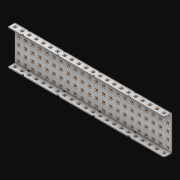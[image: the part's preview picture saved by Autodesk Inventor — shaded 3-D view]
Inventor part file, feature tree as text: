
AUTODESK INVENTOR PART (.ipt)
format: ipt  version: 2021 (Build 250183000, 183)  size: 3,487,744 bytes
history: native  units: in
note: dims shown in document units (in); Inventor stores cm internally (conversion verified against a paired STEP export)
features: extrude x155, other x154, sketch x4, thicken_offset x3, pattern_linear x3, imported_body x1
ambient origin geometry x8: Origin, YZ Plane, XZ Plane, XY Plane, X Axis, Y Axis, Z Axis, Center Point
bodies: Solid1 (feature_tree)
feature tree (320):
  thicken_offset  "Thicken1"
  thicken_offset  "Thicken2"
  thicken_offset  "Thicken3"
  pattern_linear  "Rectangular Pattern1"  Spacing1=0.001in  [1 undecoded]
  pattern_linear  "Rectangular Pattern2"  Spacing1=0.001in  [1 undecoded]
  pattern_linear  "Rectangular Pattern3"  Spacing1=0.182in  [1 undecoded]
  extrude  "Extrusion1"  Depth=0.063in TaperAngle=0.0deg
  sketch  "Sketch1"  dims[d0=0.001in]
  other  "Srf1"
  sketch  "Sketch2"  dims[d1=0.001in]
  other  "Srf2"
  sketch  "Sketch3"  dims[d2=0.001in]
  other  "Srf3"
  other  "Srf4"
  other  "Srf5"
  other  "Srf6"
  other  "Srf7"
  other  "Srf8"
  other  "Srf9"
  other  "Srf10"
  other  "Srf11"
  other  "Srf12"
  other  "Srf13"
  other  "Srf14"
  other  "Srf15"
  other  "Srf16"
  other  "Srf17"
  other  "Srf18"
  other  "Srf19"
  other  "Srf20"
  other  "Srf21"
  other  "Srf22"
  other  "Srf23"
  other  "Srf24"
  other  "Srf38"
  other  "Srf39"
  other  "Srf40"
  other  "Srf41"
  other  "Srf42"
  other  "Srf43"
  other  "Srf44"
  other  "Srf45"
  other  "Srf46"
  other  "Srf47"
  other  "Srf48"
  other  "Srf49"
  other  "Srf50"
  other  "Srf51"
  other  "Srf52"
  other  "Srf53"
  other  "Srf54"
  other  "Srf55"
  other  "Srf56"
  other  "Srf57"
  other  "Srf58"
  other  "Srf72"
  other  "Srf73"
  other  "Srf74"
  other  "Srf75"
  other  "Srf76"
  other  "Srf77"
  other  "Srf78"
  other  "Srf79"
  other  "Srf80"
  other  "Srf81"
  other  "Srf82"
  other  "Srf83"
  other  "Srf84"
  other  "Srf85"
  other  "Srf86"
  other  "Srf87"
  other  "Srf88"
  other  "Srf89"
  other  "Srf90"
  other  "Srf91"
  other  "Srf92"
  other  "Srf106"
  other  "Srf107"
  other  "Srf108"
  other  "Srf109"
  other  "Srf110"
  other  "Srf111"
  other  "Srf112"
  other  "Srf113"
  other  "Srf114"
  other  "Srf115"
  other  "Srf116"
  other  "Srf117"
  other  "Srf118"
  other  "Srf119"
  other  "Srf120"
  other  "Srf121"
  other  "Srf122"
  other  "Srf123"
  other  "Srf124"
  other  "Srf125"
  other  "Srf126"
  other  "Srf127"
  other  "Srf141"
  other  "Srf142"
  other  "Srf143"
  other  "Srf144"
  other  "Srf145"
  other  "Srf146"
  other  "Srf147"
  other  "Srf148"
  other  "Srf149"
  other  "Srf150"
  other  "Srf151"
  other  "Srf152"
  other  "Srf153"
  other  "Srf154"
  other  "Srf155"
  other  "Srf156"
  other  "Srf157"
  other  "Srf158"
  other  "Srf159"
  other  "Srf160"
  other  "Srf161"
  other  "Srf162"
  other  "Srf176"
  other  "Srf177"
  other  "Srf178"
  other  "Srf179"
  other  "Srf180"
  other  "Srf181"
  other  "Srf182"
  other  "Srf183"
  other  "Srf184"
  other  "Srf185"
  other  "Srf186"
  other  "Srf187"
  other  "Srf188"
  other  "Srf189"
  other  "Srf190"
  other  "Srf191"
  other  "Srf192"
  other  "Srf193"
  other  "Srf194"
  other  "Srf195"
  other  "Srf196"
  other  "Srf197"
  other  "Srf211"
  other  "Srf212"
  other  "Srf213"
  other  "Srf214"
  other  "Srf215"
  other  "Srf216"
  other  "Srf217"
  other  "Srf218"
  other  "Srf219"
  other  "Srf220"
  other  "Srf221"
  other  "Srf222"
  other  "Srf223"
  other  "Srf224"
  other  "Srf225"
  other  "Srf226"
  other  "Srf227"
  other  "Srf228"
  other  "Srf229"
  other  "Srf230"
  other  "Srf231"
  other  "Srf232"
  sketch  "Sketch4"  dims[d3=0.001in d4=0.001in d5=0.001in d6=0.182in d7=0.063in d8=0.0in d9=0.182in d10=0.063in d11=0.0in d12=0.182in d13=0.063in d14=0.0in d17=0.5in d18=8.6614in d20=0.5in d21=8.6614in d23=0.5in d24=1.9685in d26=0.5in d27=6.5in d28=0.0in]
  imported_body  "Imported1"
  extrude  "ExtrusionSrf1"  Depth=6.5in
  extrude  "ExtrusionSrf2"  Depth=0.063in TaperAngle=0.0deg
  extrude  "ExtrusionSrf3"  Depth=6.5in
  extrude  "ExtrusionSrf4"  Depth=0.063in TaperAngle=0.0deg
  extrude  "ExtrusionSrf5"  Depth=0.5in
  extrude  "ExtrusionSrf6"  Depth=6.5in
  extrude  "ExtrusionSrf7"  Depth=0.5in
  extrude  "ExtrusionSrf8"  Depth=6.5in
  extrude  "ExtrusionSrf9"  Depth=0.5in
  extrude  "ExtrusionSrf10"  Depth=0.5in
  extrude  "ExtrusionSrf11"  Depth=6.5in
  extrude  "ExtrusionSrf12"  TaperAngle=0.0deg  [1 undecoded]
  extrude  "ExtrusionSrf13"  [1 undecoded]
  extrude  "ExtrusionSrf14"  [1 undecoded]
  extrude  "ExtrusionSrf15"  [1 undecoded]
  extrude  "ExtrusionSrf16"  [1 undecoded]
  extrude  "ExtrusionSrf17"  [1 undecoded]
  extrude  "ExtrusionSrf18"  [1 undecoded]
  extrude  "ExtrusionSrf19"  [1 undecoded]
  extrude  "ExtrusionSrf20"  [1 undecoded]
  extrude  "ExtrusionSrf21"  [1 undecoded]
  extrude  "ExtrusionSrf22"  [1 undecoded]
  extrude  "ExtrusionSrf23"  [1 undecoded]
  extrude  "ExtrusionSrf24"  [1 undecoded]
  extrude  "ExtrusionSrf38"  [1 undecoded]
  extrude  "ExtrusionSrf39"  [1 undecoded]
  extrude  "ExtrusionSrf40"  [1 undecoded]
  extrude  "ExtrusionSrf41"  [1 undecoded]
  extrude  "ExtrusionSrf42"  [1 undecoded]
  extrude  "ExtrusionSrf43"  [1 undecoded]
  extrude  "ExtrusionSrf44"  [1 undecoded]
  extrude  "ExtrusionSrf45"  [1 undecoded]
  extrude  "ExtrusionSrf46"  [1 undecoded]
  extrude  "ExtrusionSrf47"  [1 undecoded]
  extrude  "ExtrusionSrf48"  [1 undecoded]
  extrude  "ExtrusionSrf49"  [1 undecoded]
  extrude  "ExtrusionSrf50"  [1 undecoded]
  extrude  "ExtrusionSrf51"  [1 undecoded]
  extrude  "ExtrusionSrf52"  [1 undecoded]
  extrude  "ExtrusionSrf53"  [1 undecoded]
  extrude  "ExtrusionSrf54"  [1 undecoded]
  extrude  "ExtrusionSrf55"  [1 undecoded]
  extrude  "ExtrusionSrf56"  [1 undecoded]
  extrude  "ExtrusionSrf57"  [1 undecoded]
  extrude  "ExtrusionSrf58"  [1 undecoded]
  extrude  "ExtrusionSrf72"  [1 undecoded]
  extrude  "ExtrusionSrf73"  [1 undecoded]
  extrude  "ExtrusionSrf74"  [1 undecoded]
  extrude  "ExtrusionSrf75"  [1 undecoded]
  extrude  "ExtrusionSrf76"  [1 undecoded]
  extrude  "ExtrusionSrf77"  [1 undecoded]
  extrude  "ExtrusionSrf78"  [1 undecoded]
  extrude  "ExtrusionSrf79"  [1 undecoded]
  extrude  "ExtrusionSrf80"  [1 undecoded]
  extrude  "ExtrusionSrf81"  [1 undecoded]
  extrude  "ExtrusionSrf82"  [1 undecoded]
  extrude  "ExtrusionSrf83"  [1 undecoded]
  extrude  "ExtrusionSrf84"  [1 undecoded]
  extrude  "ExtrusionSrf85"  [1 undecoded]
  extrude  "ExtrusionSrf86"  [1 undecoded]
  extrude  "ExtrusionSrf87"  [1 undecoded]
  extrude  "ExtrusionSrf88"  [1 undecoded]
  extrude  "ExtrusionSrf89"  [1 undecoded]
  extrude  "ExtrusionSrf90"  [1 undecoded]
  extrude  "ExtrusionSrf91"  [1 undecoded]
  extrude  "ExtrusionSrf92"  [1 undecoded]
  extrude  "ExtrusionSrf106"  [1 undecoded]
  extrude  "ExtrusionSrf107"  [1 undecoded]
  extrude  "ExtrusionSrf108"  [1 undecoded]
  extrude  "ExtrusionSrf109"  [1 undecoded]
  extrude  "ExtrusionSrf110"  [1 undecoded]
  extrude  "ExtrusionSrf111"  [1 undecoded]
  extrude  "ExtrusionSrf112"  [1 undecoded]
  extrude  "ExtrusionSrf113"  [1 undecoded]
  extrude  "ExtrusionSrf114"  [1 undecoded]
  extrude  "ExtrusionSrf115"  [1 undecoded]
  extrude  "ExtrusionSrf116"  [1 undecoded]
  extrude  "ExtrusionSrf117"  [1 undecoded]
  extrude  "ExtrusionSrf118"  [1 undecoded]
  extrude  "ExtrusionSrf119"  [1 undecoded]
  extrude  "ExtrusionSrf120"  [1 undecoded]
  extrude  "ExtrusionSrf121"  [1 undecoded]
  extrude  "ExtrusionSrf122"  [1 undecoded]
  extrude  "ExtrusionSrf123"  [1 undecoded]
  extrude  "ExtrusionSrf124"  [1 undecoded]
  extrude  "ExtrusionSrf125"  [1 undecoded]
  extrude  "ExtrusionSrf126"  [1 undecoded]
  extrude  "ExtrusionSrf127"  [1 undecoded]
  extrude  "ExtrusionSrf141"  [1 undecoded]
  extrude  "ExtrusionSrf142"  [1 undecoded]
  extrude  "ExtrusionSrf143"  [1 undecoded]
  extrude  "ExtrusionSrf144"  [1 undecoded]
  extrude  "ExtrusionSrf145"  [1 undecoded]
  extrude  "ExtrusionSrf146"  [1 undecoded]
  extrude  "ExtrusionSrf147"  [1 undecoded]
  extrude  "ExtrusionSrf148"  [1 undecoded]
  extrude  "ExtrusionSrf149"  [1 undecoded]
  extrude  "ExtrusionSrf150"  [1 undecoded]
  extrude  "ExtrusionSrf151"  [1 undecoded]
  extrude  "ExtrusionSrf152"  [1 undecoded]
  extrude  "ExtrusionSrf153"  [1 undecoded]
  extrude  "ExtrusionSrf154"  [1 undecoded]
  extrude  "ExtrusionSrf155"  [1 undecoded]
  extrude  "ExtrusionSrf156"  [1 undecoded]
  extrude  "ExtrusionSrf157"  [1 undecoded]
  extrude  "ExtrusionSrf158"  [1 undecoded]
  extrude  "ExtrusionSrf159"  [1 undecoded]
  extrude  "ExtrusionSrf160"  [1 undecoded]
  extrude  "ExtrusionSrf161"  [1 undecoded]
  extrude  "ExtrusionSrf162"  [1 undecoded]
  extrude  "ExtrusionSrf176"  [1 undecoded]
  extrude  "ExtrusionSrf177"  [1 undecoded]
  extrude  "ExtrusionSrf178"  [1 undecoded]
  extrude  "ExtrusionSrf179"  [1 undecoded]
  extrude  "ExtrusionSrf180"  [1 undecoded]
  extrude  "ExtrusionSrf181"  [1 undecoded]
  extrude  "ExtrusionSrf182"  [1 undecoded]
  extrude  "ExtrusionSrf183"  [1 undecoded]
  extrude  "ExtrusionSrf184"  [1 undecoded]
  extrude  "ExtrusionSrf185"  [1 undecoded]
  extrude  "ExtrusionSrf186"  [1 undecoded]
  extrude  "ExtrusionSrf187"  [1 undecoded]
  extrude  "ExtrusionSrf188"  [1 undecoded]
  extrude  "ExtrusionSrf189"  [1 undecoded]
  extrude  "ExtrusionSrf190"  [1 undecoded]
  extrude  "ExtrusionSrf191"  [1 undecoded]
  extrude  "ExtrusionSrf192"  [1 undecoded]
  extrude  "ExtrusionSrf193"  [1 undecoded]
  extrude  "ExtrusionSrf194"  [1 undecoded]
  extrude  "ExtrusionSrf195"  [1 undecoded]
  extrude  "ExtrusionSrf196"  [1 undecoded]
  extrude  "ExtrusionSrf197"  [1 undecoded]
  extrude  "ExtrusionSrf211"  [1 undecoded]
  extrude  "ExtrusionSrf212"  [1 undecoded]
  extrude  "ExtrusionSrf213"  [1 undecoded]
  extrude  "ExtrusionSrf214"  [1 undecoded]
  extrude  "ExtrusionSrf215"  [1 undecoded]
  extrude  "ExtrusionSrf216"  [1 undecoded]
  extrude  "ExtrusionSrf217"  [1 undecoded]
  extrude  "ExtrusionSrf218"  [1 undecoded]
  extrude  "ExtrusionSrf219"  [1 undecoded]
  extrude  "ExtrusionSrf220"  [1 undecoded]
  extrude  "ExtrusionSrf221"  [1 undecoded]
  extrude  "ExtrusionSrf222"  [1 undecoded]
  extrude  "ExtrusionSrf223"  [1 undecoded]
  extrude  "ExtrusionSrf224"  [1 undecoded]
  extrude  "ExtrusionSrf225"  [1 undecoded]
  extrude  "ExtrusionSrf226"  [1 undecoded]
  extrude  "ExtrusionSrf227"  [1 undecoded]
  extrude  "ExtrusionSrf228"  [1 undecoded]
  extrude  "ExtrusionSrf229"  [1 undecoded]
  extrude  "ExtrusionSrf230"  [1 undecoded]
  extrude  "ExtrusionSrf231"  [1 undecoded]
  extrude  "ExtrusionSrf232"  [1 undecoded]
note: 146 required parameter values undecoded (feature->parameter linkage not recoverable at this tier; creation-order binding heuristic only, values carry confidence <= 0.55)
